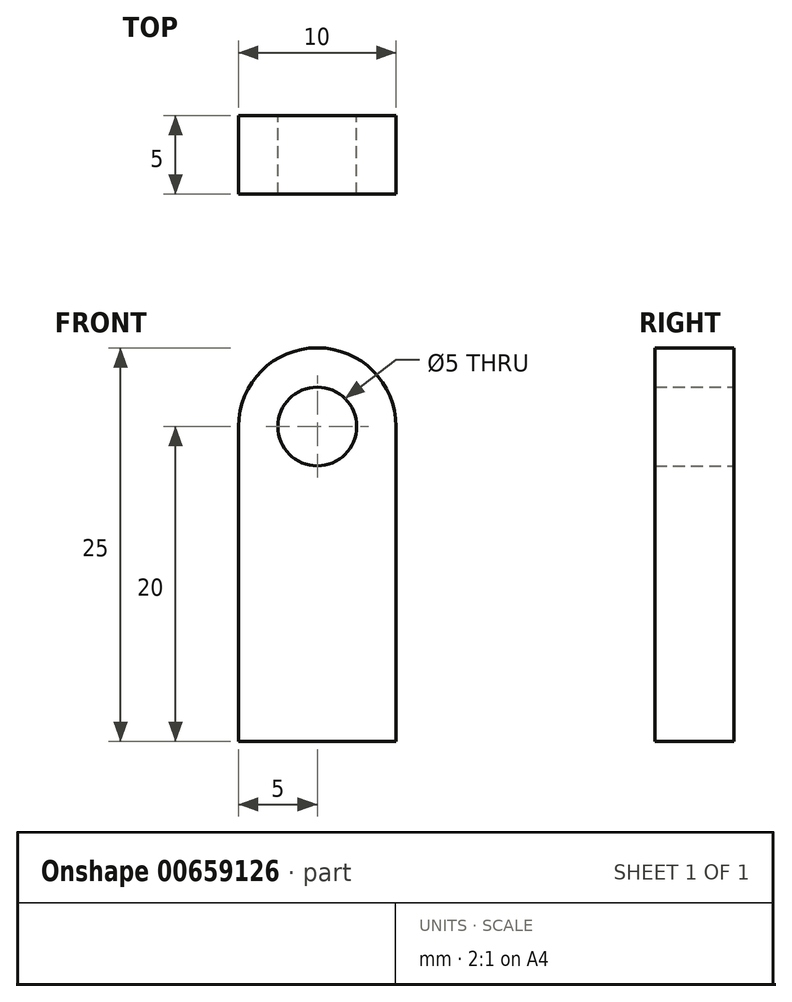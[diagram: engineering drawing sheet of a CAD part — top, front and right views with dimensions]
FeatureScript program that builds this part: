
annotation { "Feature Type Name" : "Feature", "Feature Type Description" : "" }
export const myFeature = defineFeature(function(context is Context, id is Id, definition is map)
    precondition{}
    {
        {
            var Q0;
            Q0=qCreatedBy(makeId("Front.planeOp"),FACE);
            var sketch = newSketch(context, id + "F0", { "sketchPlane" : qUnion([Q0])});
            skLineSegment(sketch, "E0", {"start": v(-5, -20) * mm, "end": v(-5, 0) * mm});
            skArc(sketch, "E1", {"start": v(-5, 0) * mm, "mid": v(0, 5) * mm, "end": v(5, 0) * mm});
            skLineSegment(sketch, "E2", {"start": v(5, 0) * mm, "end": v(5, -20) * mm});
            skLineSegment(sketch, "E3", {"start": v(5, -20) * mm, "end": v(-5, -20) * mm});
            skCircle(sketch, "E4", {"center": v(0, 0) * mm, "radius": 2.5 * mm});
            skSolve(sketch);
        }
        {
            var Q0;
            Q0=makeQuery(id+"F0.imprint","IMPRINT",FACE,{"disambiguationData":[TD([[makeQuery(id+"F0.imprint","IMPRINT",EDGE,{"derivedFrom":sQuery(id+"F0.wireOp",EDGE,"E0")}),-1.0]])]});
            extrude(context, id + "F1", {"entities" : qUnion([Q0]), "depth" : 5 * mm, "offsetDistance" : 25 * mm});
        }
    });
